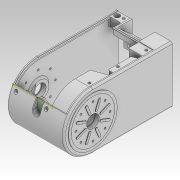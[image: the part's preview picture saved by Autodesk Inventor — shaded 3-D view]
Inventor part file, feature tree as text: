
AUTODESK INVENTOR PART (.ipt)
format: ipt  version: 2020 (Build 240168000, 168)  size: 1,221,120 bytes
history: native  units: mm
features: extrude x55, sketch x55, projected_geometry x9, fillet x8, plane x7, chamfer x5, pattern_circular x2, revolve x2, loft x1, other x1
ambient origin geometry x8: Origin, YZ Plane, XZ Plane, XY Plane, X Axis, Y Axis, Z Axis, Center Point
bodies: Solid1 (feature_tree)
feature tree (145):
  extrude  "Extrusion1"  Depth=250.0mm
  extrude  "Extrusion2"  Depth=100.0mm TaperAngle=0.0deg
  extrude  "Extrusion3"  TaperAngle=0.0deg  [1 undecoded]
  extrude  "Extrusion4"  Depth=10.0mm
  extrude  "Extrusion5"  Depth=30.0mm
  pattern_circular  "Circular Pattern1"  Count=8 Angle=360.0deg
  plane  "Work Plane1"
  plane  "Work Plane2"
  extrude  "Extrusion6"  Depth=30.0mm
  extrude  "Extrusion7"  Depth=10.0mm
  extrude  "Extrusion8"  Depth=10.0mm
  extrude  "Extrusion9"  [1 undecoded]
  chamfer  "Chamfer1"  Distance=10.0mm
  extrude  "Extrusion13"  Depth=10.0mm TaperAngle=0.0deg
  extrude  "Extrusion14"  Depth=3.0mm TaperAngle=0.0deg
  extrude  "Extrusion15"  Depth=3.0mm
  extrude  "Extrusion16"  Depth=3.0mm
  extrude  "Extrusion17"  Depth=80.0mm
  extrude  "Extrusion18"  Depth=60.0mm
  extrude  "Extrusion19"  Depth=80.0mm TaperAngle=360.0deg
  extrude  "Extrusion20"  Depth=15.5mm TaperAngle=0.0deg
  fillet  "Fillet2"  Radius=22.1mm
  pattern_circular  "Circular Pattern2"  Count=8 Angle=360.0deg
  extrude  "Extrusion21"  Depth=10.0mm
  extrude  "Extrusion22"  Depth=7.0mm
  plane  "Work Plane3"
  revolve  "Revolution1"  [1 undecoded]
  revolve  "Revolution2"  [1 undecoded]
  plane  "Work Plane4"
  extrude  "Extrusion23"  Depth=96.8mm TaperAngle=0.0deg
  extrude  "Extrusion24"  Depth=2.5mm
  fillet  "Fillet3"  Radius=5.2mm
  loft  "Loft1"
  extrude  "Extrusion25"  TaperAngle=90.0deg  [1 undecoded]
  extrude  "Extrusion26"  Depth=15.0mm
  extrude  "Extrusion27"  Depth=19.0mm
  extrude  "Extrusion28"  Depth=2.7mm
  plane  "Work Plane5"
  extrude  "Extrusion29"  Depth=4.0mm
  extrude  "Extrusion30"  TaperAngle=90.0deg  [1 undecoded]
  extrude  "Extrusion32"  Depth=18.8mm TaperAngle=0.0deg
  extrude  "Extrusion35"  Depth=6.0mm
  extrude  "Extrusion36"  Depth=4.0mm
  extrude  "Extrusion37"  [1 undecoded]
  chamfer  "Chamfer3"  Distance=1.0mm
  plane  "Work Plane8"
  extrude  "Extrusion38"  Depth=5.0mm
  extrude  "Extrusion39"  TaperAngle=0.0deg  [1 undecoded]
  fillet  "Fillet5"  [1 undecoded]
  extrude  "Extrusion40"  Depth=10.0mm TaperAngle=0.0deg
  chamfer  "Chamfer4"  [1 undecoded]
  chamfer  "Chamfer5"  Distance=255.0mm
  extrude  "Extrusion41"  Depth=5.0mm
  extrude  "Extrusion42"  Depth=12.0mm
  chamfer  "Chamfer6"  Distance=64.0mm
  fillet  "Fillet6"  Radius=3.0mm
  fillet  "Fillet7"  Radius=5.0mm
  extrude  "Extrusion43"  Depth=5.0mm
  extrude  "Extrusion44"  Depth=3.0mm
  extrude  "Extrusion45"  Depth=10.0mm TaperAngle=0.0deg
  extrude  "Extrusion46"  Depth=3.0mm TaperAngle=45.0deg
  extrude  "Extrusion47"  Depth=3.0mm
  extrude  "Extrusion48"  Depth=0.25mm
  fillet  "Fillet8"  Radius=17.25mm
  extrude  "Extrusion49"  Depth=3.0mm
  extrude  "Extrusion50"  Depth=15.0mm
  extrude  "Extrusion51"  Depth=3.0mm
  fillet  "Fillet9"  Radius=3.8mm
  extrude  "Extrusion52"  Depth=3.0mm TaperAngle=0.0deg
  extrude  "Extrusion54"  Depth=3.0mm
  sketch  "Sketch62"  dims[d155=110.0mm d156=0.0mm d157=0.0mm]
  extrude  "Extrusion55"  Depth=3.0mm TaperAngle=0.0deg
  extrude  "Extrusion56"  Depth=3.0mm
  extrude  "Extrusion57"  Depth=3.0mm
  extrude  "Extrusion58"  Depth=3.0mm
  plane  "Work Plane10"
  extrude  "Extrusion59"  Depth=3.0mm
  extrude  "Extrusion60"  Depth=3.0mm TaperAngle=0.0deg
  extrude  "Extrusion61"  Depth=3.0mm
  fillet  "Fillet10"  Radius=2.0mm
  extrude  "Extrusion62"  Depth=3.0mm
  sketch  "Sketch1"  dims[d0=50.0mm d1=250.0mm]
  sketch  "Sketch2"  dims[d2=50.0mm d3=100.0mm d4=0.0mm]
  sketch  "Sketch4"  dims[d5=5.0mm d7=0.0mm d8=0.0mm]
  sketch  "Sketch5"  dims[d11=10.0mm d12=0.0mm d14=85.0mm]
  sketch  "Sketch7"  dims[d15=1.0mm d16=0.0mm d17=30.0mm]
  projected_geometry  "Projected Loop1"
  sketch  "Sketch8"  dims[d18=3.3mm]
  projected_geometry  "Projected Loop2"
  projected_geometry  "Projected Loop4"
  sketch  "Sketch9"  dims[d19=15.0mm d20=0.0mm d21=80.0mm d22=360.0deg]
  sketch  "Sketch10"  dims[d24=30.0mm d25=30.0mm]
  sketch  "Sketch14"  dims[d30=-5.0mm d31=10.0mm]
  sketch  "Sketch15"  dims[d32=10.0mm d33=10.0mm]
  sketch  "Sketch16"  dims[d34=31.5mm d35=0.0mm d36=-5.0mm d38=10.0mm d39=0.0mm]
  sketch  "Sketch17"  dims[d40=22.1mm d41=10.0mm d42=0.0mm]
  sketch  "Sketch18"  dims[d43=5.0mm d44=3.0mm d45=0.0mm]
  sketch  "Sketch19"  dims[d56=3.0mm d57=2.0mm d58=45.0deg d62=95.1mm]
  sketch  "Sketch20"  dims[d63=10.0mm d64=0.0mm d65=3.0mm]
  sketch  "Sketch21"  dims[d66=0.5mm d67=0.0mm d68=80.0mm]
  sketch  "Sketch22"  dims[d69=15.5mm d70=0.0mm d71=60.0mm]
  sketch  "Sketch23"  dims[d72=3.2mm d73=80.0mm d75=360.0deg]
  other  "Work Axis1"
  sketch  "Sketch24"  dims[d77=15.5mm d78=0.0mm d79=15.5mm d80=0.0mm d81=22.1mm]
  projected_geometry  "Projected Loop5"
  projected_geometry  "Projected Loop6"
  sketch  "Sketch26"  dims[d82=0.0mm d83=0.0mm]
  sketch  "Sketch27"  dims[d84=76.0mm]
  sketch  "Sketch28"  dims[d85=0.1mm d86=0.0mm]
  sketch  "Sketch29"  dims[d87=15.0mm]
  sketch  "Sketch30"  dims[d88=2.0mm]
  sketch  "Sketch31"  dims[d89=22.5mm]
  sketch  "Sketch32"  dims[d90=0.8mm d91=0.0mm]
  sketch  "Sketch33"  dims[d92=0.2mm d93=80.0mm d94=360.0deg]
  projected_geometry  "Projected Loop7"
  sketch  "Sketch34"  dims[d96=24.43461mm d97=10.0mm]
  sketch  "Sketch35"  dims[d98=6.1mm d99=7.0mm]
  sketch  "Sketch38"  dims[d100=6.1mm d101=7.0mm]
  projected_geometry  "Projected Loop8"
  sketch  "Sketch42"  dims[d102=5.0mm d103=0.0mm d104=25.0mm]
  sketch  "Sketch43"  dims[d105=16.1mm d106=96.8mm d107=0.0mm]
  sketch  "Sketch45"  dims[d108=0.0mm d109=2.5mm d110=5.2mm]
  projected_geometry  "Projected Loop9"
  sketch  "Sketch46"  dims[d111=1.0mm d112=5.0mm]
  sketch  "Sketch47"  dims[d113=5.2mm d114=90.0deg]
  sketch  "Sketch48"  dims[d115=15.0mm d116=25.0mm]
  sketch  "Sketch49"  dims[d117=25.0mm d118=19.0mm]
  sketch  "Sketch50"  dims[d119=19.0mm d120=2.7mm]
  projected_geometry  "Projected Loop10"
  sketch  "Sketch51"  dims[d122=4.0mm d123=0.0mm d124=5.5mm]
  sketch  "Sketch52"  dims[d125=2.0mm d126=0.0mm d127=90.0deg]
  sketch  "Sketch53"  dims[d128=2.0mm d129=18.8mm d130=0.0mm]
  sketch  "Sketch54"  dims[d131=111.25mm d132=0.0mm d133=6.0mm]
  sketch  "Sketch55"  dims[d134=4.0mm d135=0.0mm d136=1.0mm]
  sketch  "Sketch56"  dims[d137=1.0mm d138=0.0mm d139=-7.0mm]
  sketch  "Sketch57"  dims[d140=1.0mm d141=1.0mm d142=0.0mm]
  sketch  "Sketch58"  dims[d143=7.0mm d144=5.0mm]
  sketch  "Sketch59"  dims[d145=6.0mm d146=0.0mm d147=90.0deg d148=0.0mm d149=90.0deg]
  sketch  "Sketch61"  dims[d150=3.0mm d151=10.0mm d152=0.0mm]
  sketch  "Sketch63"  dims[d159=30.0deg]
  sketch  "Sketch64"  dims[d160=6.0mm d177=255.0mm d178=0.0mm]
  sketch  "Sketch65"  dims[d179=2.1mm d180=5.0mm]
  sketch  "Sketch66"  dims[d181=42.0mm d182=0.0mm d183=12.0mm]
  sketch  "Sketch67"  dims[d184=78.0mm]
  sketch  "Sketch68"  dims[d185=45.0mm d186=64.0mm d187=3.0mm d188=0.0mm d189=5.0mm d190=5.0mm d191=4.3mm d192=10.0mm d193=0.0mm d194=3.0mm d195=2.0mm d196=45.0deg d199=23.0mm d200=0.25mm d201=17.25mm d202=0.0mm d203=58.0mm d204=15.0mm d205=61.8mm d206=3.8mm d207=8.0mm d208=0.0mm d209=2.0mm d210=20.75mm d211=0.0mm d212=1.0mm d213=7.0mm d214=2.0mm d215=3.490659mm d216=7.0mm d217=2.0mm d218=3.490659mm d219=1.0mm d220=90.0mm d221=0.0mm d222=2.0mm d223=2.0mm d224=0.0mm d225=2.0mm d226=2.0mm d227=3.490659mm d228=2.0mm d229=3.0mm d230=2.0mm d231=10.0mm d232=0.0mm d233=2.0mm d234=0.5mm d235=45.0deg d236=10.0mm d237=0.0mm d238=5.0mm d239=10.0mm d240=10.0mm d241=0.0mm d242=30.0mm d243=3.5mm d244=12.0mm d245=10.0mm d246=0.0mm d247=5.5mm d248=3.0mm d249=0.0mm d250=30.0mm d251=6.0mm d252=10.0mm d253=0.0mm d254=1.0mm d255=15.0mm d256=15.0mm d257=10.0mm d258=0.0mm d259=4.0mm d260=5.5mm d261=10.0mm d262=0.0mm d263=9.0mm d264=5.0mm d265=0.0mm d266=2.0mm d267=0.2mm d268=0.0mm d274=58.0mm d275=58.0mm d276=9.0mm d277=9.0mm d278=9.0mm d279=9.0mm d280=9.0mm d281=9.0mm d282=9.0mm d283=9.0mm d284=0.5mm d285=15.0mm d286=0.0mm d287=7.0mm d288=3.5mm d289=5.0mm d290=0.0mm d291=5.0mm d292=0.0mm d293=6.0mm d294=6.0mm d295=6.0mm d296=6.0mm d297=6.0mm d298=4.3mm d299=10.0mm d300=0.0mm d301=6.0mm d302=6.0mm d303=6.0mm d304=6.0mm d305=3.2mm d306=10.0mm d307=0.0mm d308=-2.5mm d309=6.0mm d310=10.0mm d311=0.0mm d312=3.490659mm d313=3.490659mm d314=10.0mm d315=0.0mm d316=10.0mm d317=0.0mm d318=3.0mm d319=0.2mm d320=0.0mm d321=0.5mm d322=0.872665mm]
note: 10 required parameter values undecoded (feature->parameter linkage not recoverable at this tier; creation-order binding heuristic only, values carry confidence <= 0.55)